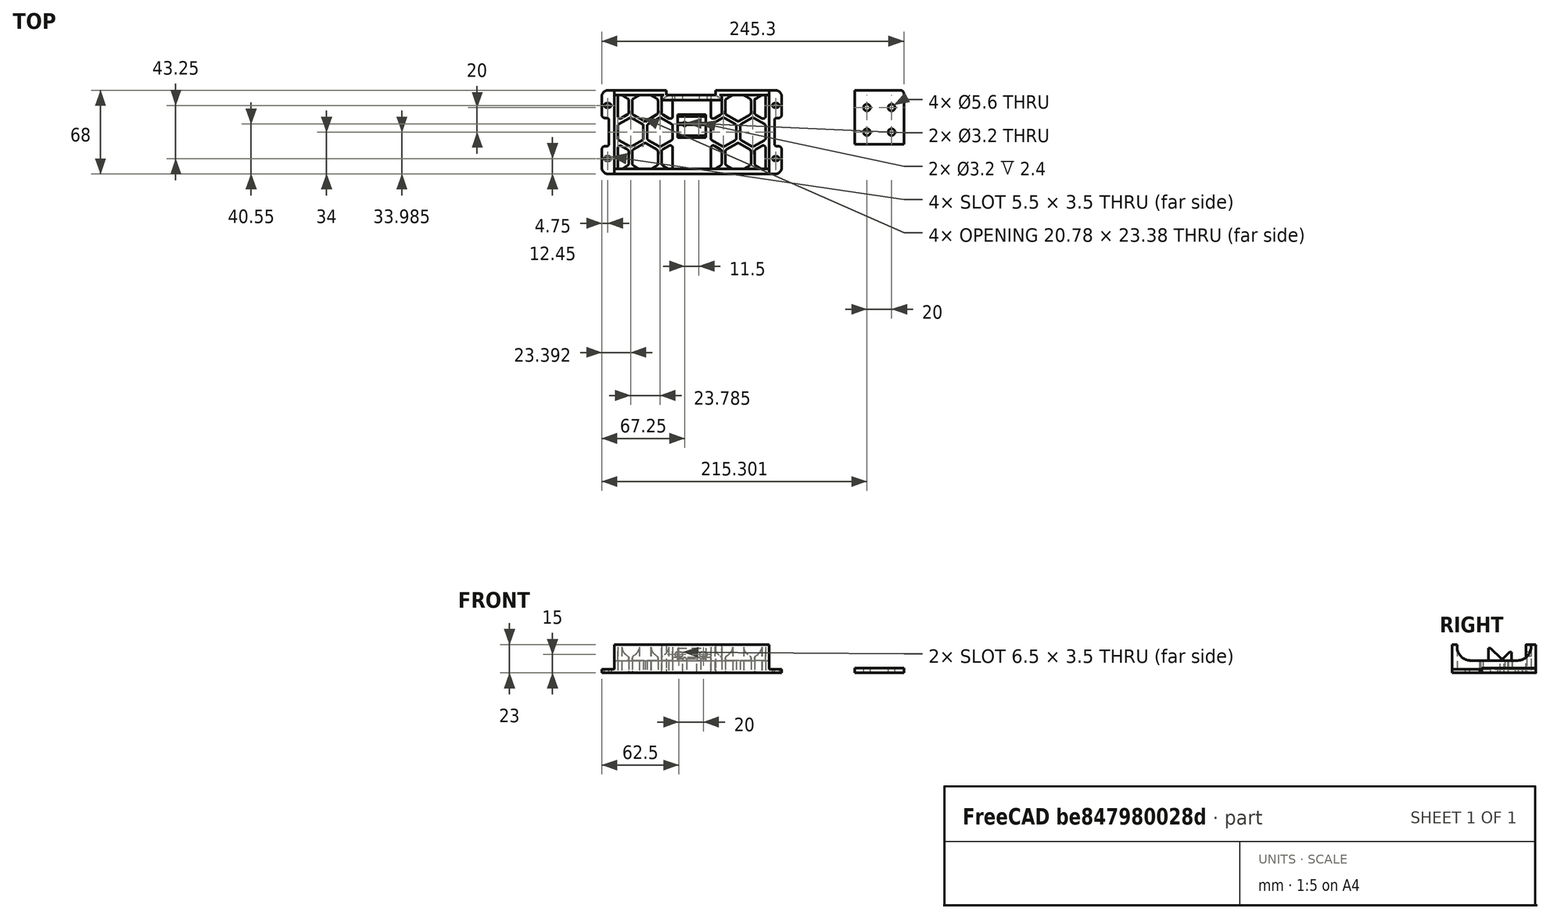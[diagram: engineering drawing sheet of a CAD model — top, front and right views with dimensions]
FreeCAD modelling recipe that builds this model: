
FCSTD DOCUMENT  (FreeCAD 0.19R24291 (Git))
Label: Middle Grill V2
License: All rights reserved
LicenseURL: http://en.wikipedia.org/wiki/All_rights_reserved
objects: Sketcher::SketchObject×10, PartDesign::Pad×5, PartDesign::Pocket×5, Mesh::Feature×4, PartDesign::Body×3, App::DocumentObjectGroup×1, PartDesign::Fillet×1
note: 35 computed .brp shape members not serialized (recipe doc carries the construction recipe); baked Part::Feature solids carry a one-line shape summary decoded from their .brp

FEATURE [Mesh::Feature] grill_front_middle
  Placement = pos=(-37.5,-76,0) rot=(0,0,1;0rad)
FEATURE [Mesh::Feature] grill_front_middle001
  Placement = pos=(-60,-73.5,0) rot=(0,0,1;0rad)
FEATURE [Sketcher::SketchObject] Sketch
  FullyConstrained = true
  MapMode = 5
  Support = -> [XY_Plane]
  sketch-geometry (43):
    g0: LineSegment StartX=5 StartY=0 StartZ=0 EndX=141 EndY=0 EndZ=0
    g1: LineSegment StartX=0 StartY=63 StartZ=0 EndX=0 EndY=48 EndZ=0
    g2: LineSegment StartX=141 StartY=68 StartZ=0 EndX=5 EndY=68 EndZ=0
    g3: ArcOfCircle CenterX=5 CenterY=63 CenterZ=0 NormalX=0 NormalY=0 NormalZ=1 AngleXU=0 Radius=5 StartAngle=1.5708 EndAngle=3.14159
    g4: ArcOfCircle CenterX=5 CenterY=5 CenterZ=0 NormalX=0 NormalY=0 NormalZ=1 AngleXU=0 Radius=5 StartAngle=3.14159 EndAngle=4.71239
    g5: LineSegment StartX=146 StartY=63 StartZ=0 EndX=146 EndY=48 EndZ=0
    g6: ArcOfCircle CenterX=141 CenterY=5 CenterZ=0 NormalX=0 NormalY=0 NormalZ=1 AngleXU=0 Radius=5 StartAngle=4.71239 EndAngle=6.28319
    g7: ArcOfCircle CenterX=141 CenterY=63 CenterZ=0 NormalX=0 NormalY=0 NormalZ=1 AngleXU=0 Radius=5 StartAngle=-9e-16 EndAngle=1.5708
    g8: LineSegment StartX=0 StartY=20 StartZ=0 EndX=0 EndY=5 EndZ=0
    g9: LineSegment StartX=2.5 StartY=22.5 StartZ=0 EndX=4.1 EndY=22.5 EndZ=0
    g10: LineSegment StartX=5.6 StartY=24 StartZ=0 EndX=5.6 EndY=44 EndZ=0
    g11: LineSegment StartX=4.1 StartY=45.5 StartZ=0 EndX=2.5 EndY=45.5 EndZ=0
    g12: ArcOfCircle CenterX=2.5 CenterY=48 CenterZ=0 NormalX=0 NormalY=0 NormalZ=1 AngleXU=0 Radius=2.5 StartAngle=3.14159 EndAngle=4.71239
    g13: ArcOfCircle CenterX=4.1 CenterY=44 CenterZ=0 NormalX=0 NormalY=0 NormalZ=1 AngleXU=0 Radius=1.5 StartAngle=-1.8e-15 EndAngle=1.5708
    g14: ArcOfCircle CenterX=4.1 CenterY=24 CenterZ=0 NormalX=0 NormalY=0 NormalZ=1 AngleXU=0 Radius=1.5 StartAngle=4.71239 EndAngle=6.28319
    g15: ArcOfCircle CenterX=2.5 CenterY=20 CenterZ=0 NormalX=0 NormalY=0 NormalZ=1 AngleXU=0 Radius=2.5 StartAngle=1.5708 EndAngle=3.14159
    g16: LineSegment StartX=143.5 StartY=45.5 StartZ=0 EndX=141.9 EndY=45.5 EndZ=0
    g17: LineSegment StartX=140.4 StartY=44 StartZ=0 EndX=140.4 EndY=24 EndZ=0
    g18: LineSegment StartX=141.9 StartY=22.5 StartZ=0 EndX=143.5 EndY=22.5 EndZ=0
    g19: ArcOfCircle CenterX=143.5 CenterY=48 CenterZ=0 NormalX=0 NormalY=0 NormalZ=1 AngleXU=0 Radius=2.5 StartAngle=4.71239 EndAngle=6.28319
    g20: ArcOfCircle CenterX=141.9 CenterY=44 CenterZ=0 NormalX=0 NormalY=0 NormalZ=1 AngleXU=0 Radius=1.5 StartAngle=1.5708 EndAngle=3.14159
    g21: LineSegment StartX=146 StartY=20 StartZ=0 EndX=146 EndY=5 EndZ=0
    g22: ArcOfCircle CenterX=141.9 CenterY=24 CenterZ=0 NormalX=0 NormalY=0 NormalZ=1 AngleXU=0 Radius=1.5 StartAngle=3.14159 EndAngle=4.71239
    g23: ArcOfCircle CenterX=143.5 CenterY=20 CenterZ=0 NormalX=0 NormalY=0 NormalZ=1 AngleXU=0 Radius=2.5 StartAngle=1e-16 EndAngle=1.5708
    g24: ArcOfCircle CenterX=3.75 CenterY=55.7 CenterZ=0 NormalX=0 NormalY=0 NormalZ=1 AngleXU=0 Radius=1.75 StartAngle=1.5708 EndAngle=4.71239
    g25: ArcOfCircle CenterX=5.75 CenterY=55.7 CenterZ=0 NormalX=0 NormalY=0 NormalZ=1 AngleXU=0 Radius=1.75 StartAngle=4.71239 EndAngle=7.85398
    g26: LineSegment StartX=3.75 StartY=53.95 StartZ=0 EndX=5.75 EndY=53.95 EndZ=0
    g27: LineSegment StartX=3.75 StartY=57.45 StartZ=0 EndX=5.75 EndY=57.45 EndZ=0
    g28: ArcOfCircle CenterX=140.25 CenterY=55.7 CenterZ=0 NormalX=0 NormalY=0 NormalZ=1 AngleXU=0 Radius=1.75 StartAngle=1.5708 EndAngle=4.71239
    g29: ArcOfCircle CenterX=142.25 CenterY=55.7 CenterZ=0 NormalX=0 NormalY=0 NormalZ=1 AngleXU=0 Radius=1.75 StartAngle=4.71239 EndAngle=7.85398
    g30: LineSegment StartX=140.25 StartY=53.95 StartZ=0 EndX=142.25 EndY=53.95 EndZ=0
    g31: LineSegment StartX=140.25 StartY=57.45 StartZ=0 EndX=142.25 EndY=57.45 EndZ=0
    g32: LineSegment StartX=3.75 StartY=57.45 StartZ=0 EndX=140.25 EndY=57.45 EndZ=0
    g33: ArcOfCircle CenterX=3.75 CenterY=12.45 CenterZ=0 NormalX=0 NormalY=0 NormalZ=1 AngleXU=0 Radius=1.75 StartAngle=1.5708 EndAngle=4.71239
    g34: ArcOfCircle CenterX=5.75 CenterY=12.45 CenterZ=0 NormalX=0 NormalY=0 NormalZ=1 AngleXU=0 Radius=1.75 StartAngle=4.71239 EndAngle=7.85398
    g35: LineSegment StartX=3.75 StartY=10.7 StartZ=0 EndX=5.75 EndY=10.7 EndZ=0
    g36: LineSegment StartX=3.75 StartY=14.2 StartZ=0 EndX=5.75 EndY=14.2 EndZ=0
    g37: LineSegment StartX=3.75 StartY=57.45 StartZ=0 EndX=3.75 EndY=14.2 EndZ=0
    g38: ArcOfCircle CenterX=140.25 CenterY=12.45 CenterZ=0 NormalX=0 NormalY=0 NormalZ=1 AngleXU=0 Radius=1.75 StartAngle=1.5708 EndAngle=4.71239
    g39: ArcOfCircle CenterX=142.25 CenterY=12.45 CenterZ=0 NormalX=0 NormalY=0 NormalZ=1 AngleXU=0 Radius=1.75 StartAngle=4.71239 EndAngle=7.85398
    g40: LineSegment StartX=140.25 StartY=10.7 StartZ=0 EndX=142.25 EndY=10.7 EndZ=0
    g41: LineSegment StartX=140.25 StartY=14.2 StartZ=0 EndX=142.25 EndY=14.2 EndZ=0
    g42: LineSegment StartX=3.75 StartY=14.2 StartZ=0 EndX=140.25 EndY=14.2 EndZ=0
  constraints (108):
    c: Horizontal(g0)
    c: Vertical(g1)
    c: Tangent(g1,g3) = -1.5708
    c: Tangent(g2,g3) = -1.5708
    c: Coincident(g8,g4) = -1.5708
    c: Tangent(g0,g4) = -1.5708
    c: PointOnObject(g0,g-1)
    c: PointOnObject(g1,g-2)
    c: DistanceY(g-1,g2) = 68
    c: Radius(g3) = 5
    c: Equal(g3,g4)
    c: Vertical(g5)
    c: Tangent(g0,g6) = -1.5708
    c: Tangent(g5,g7) = 1.5708
    c: Equal(g3,g7)
    c: Equal(g7,g6)
    c: Tangent(g1,g8)
    c: Horizontal(g9)
    c: Vertical(g10)
    c: Horizontal(g11)
    c: Tangent(g1,g12) = -1.5708
    c: Tangent(g11,g12) = 1.5708
    c: Tangent(g11,g13) = -1.5708
    c: Tangent(g10,g13) = -1.5708
    c: Tangent(g10,g14) = -1.5708
    c: Tangent(g9,g14) = -1.5708
    c: Tangent(g9,g15) = 1.5708
    c: Tangent(g8,g15) = -1.5708
    c: Radius(g13) = 1.5
    c: Equal(g13,g14)
    c: Radius(g15) = 2.5
    c: Equal(g15,g12)
    c: DistanceY(g10,g10) = 20
    c: DistanceX(g11,g11) = 1.6
    c: Equal(g8,g1)
    c: Angle(g4) = 1.5708
    c: Vertical(g17)
    c: Horizontal(g16)
    c: Tangent(g16,g19) = 1.5708
    c: Tangent(g5,g19) = 1.5708
    c: Tangent(g16,g20) = -1.5708
    c: Tangent(g17,g20) = -1.5708
    c: Horizontal(g18)
    c: Coincident(g21,g6)
    c: Vertical(g21)
    c: Tangent(g17,g22) = -1.5708
    c: Tangent(g18,g22) = -1.5708
    c: Tangent(g18,g23) = 1.5708
    c: Tangent(g21,g23) = 1.5708
    c: Equal(g12,g19)
    c: Equal(g19,g23)
    c: Equal(g13,g20)
    c: Equal(g20,g22)
    c: Equal(g10,g17)
    c: Equal(g5,g21)
    c: Angle(g6) = 1.5708
    c: DistanceX(g16,g16) = 1.6
    c: Equal(g16,g18)
    c: Tangent(g24,g27) = 1.5708
    c: Tangent(g24,g26) = -1.5708
    c: Tangent(g26,g25) = -1.5708
    c: Tangent(g27,g25) = 1.5708
    c: Horizontal(g26)
    c: Equal(g24,g25)
    c: DistanceY(g-1,g24) = 55.7
    c: DistanceX(g24,g25) = 2
    c: DistanceX(g1,g24) = 3.75
    c: Radius(g25) = 1.75
    c: Tangent(g28,g31) = 1.5708
    c: Tangent(g28,g30) = -1.5708
    c: Tangent(g30,g29) = -1.5708
    c: Tangent(g31,g29) = 1.5708
    c: Horizontal(g30)
    c: Equal(g28,g29)
    c: DistanceX(g28,g29) = 2
    c: Radius(g29) = 1.75
    c: Coincident(g24,g32)
    c: Coincident(g28,g32)
    c: Distance(g32) = 136.5
    c: Angle(g32) = 0
    c: Tangent(g33,g36) = 1.5708
    c: Tangent(g33,g35) = -1.5708
    c: Tangent(g35,g34) = -1.5708
    c: Tangent(g36,g34) = 1.5708
    c: Horizontal(g35)
    c: Equal(g33,g34)
    c: DistanceX(g33,g34) = 2
    c: Radius(g34) = 1.75
    c: Coincident(g24,g37)
    c: Coincident(g33,g37)
    c: Distance(g37) = 43.25
    c: Perpendicular(g37,g32)
    c: Tangent(g38,g41) = 1.5708
    c: Tangent(g38,g40) = -1.5708
    c: Tangent(g40,g39) = -1.5708
    c: Tangent(g41,g39) = 1.5708
    c: Horizontal(g40)
    c: Equal(g38,g39)
    c: DistanceX(g38,g39) = 2
    c: Radius(g39) = 1.75
    c: Coincident(g33,g42)
    c: Coincident(g38,g42)
    c: Equal(g32,g42)
    c: Parallel(g42,g32)
    c: Coincident(g2,g7)
    c: Horizontal(g2)
    c: DistanceX(g2,g2) = 136
    c: Equal(g2,g0)
FEATURE [PartDesign::Pad] Pad  label="Base pad"
  Direction = (1,1,1)
  Length = 3
  Length2 = 100
  Profile = -> Sketch
  Type = 0
FEATURE [Sketcher::SketchObject] Sketch001
  ExternalGeometry = -> [Pad]
  FullyConstrained = true
  MapMode = 5
  Placement = pos=(0,0,3) rot=(0,0,1;0rad)
  Support = -> [Pad]
  sketch-geometry (4):
    g0: LineSegment StartX=10 StartY=68 StartZ=0 EndX=136 EndY=68 EndZ=0
    g1: LineSegment StartX=136 StartY=68 StartZ=0 EndX=136 EndY=0 EndZ=0
    g2: LineSegment StartX=136 StartY=0 StartZ=0 EndX=10 EndY=0 EndZ=0
    g3: LineSegment StartX=10 StartY=0 StartZ=0 EndX=10 EndY=68 EndZ=0
  constraints (13):
    c: Coincident(g0,g1)
    c: Coincident(g1,g2)
    c: Coincident(g2,g3)
    c: Coincident(g3,g0)
    c: Horizontal(g0)
    c: Horizontal(g2)
    c: Vertical(g1)
    c: Vertical(g3)
    c: PointOnObject(g0,g-3)
    c: PointOnObject(g1,g-1)
    c: DistanceX(g-1,g2) = 10
    c: DistanceX(g1,g-4) = 10
    c: DistanceX(g-1,g-4) = 146
FEATURE [PartDesign::Pad] Pad001
  BaseFeature = -> Pad
  Direction = (1,1,1)
  Length = 20
  Length2 = 100
  Profile = -> Sketch001
  Type = 0
FEATURE [Sketcher::SketchObject] Sketch002
  ExternalGeometry = -> [Pad001]
  FullyConstrained = true
  MapMode = 5
  Placement = pos=(10,0,0) rot=(0.57735,-0.57735,-0.57735;2.0944rad)
  Support = -> [Pad001]
  sketch-geometry (6):
    g0: LineSegment StartX=-64 StartY=23 StartZ=0 EndX=-4 EndY=23 EndZ=0
    g1: LineSegment StartX=-4 StartY=23 StartZ=0 EndX=-4 EndY=21 EndZ=0
    g2: LineSegment StartX=-15 StartY=10 StartZ=0 EndX=-53 EndY=10 EndZ=0
    g3: LineSegment StartX=-64 StartY=21 StartZ=0 EndX=-64 EndY=23 EndZ=0
    g4: ArcOfCircle CenterX=-53 CenterY=21 CenterZ=0 NormalX=0 NormalY=0 NormalZ=1 AngleXU=0 Radius=11 StartAngle=3.14159 EndAngle=4.71239
    g5: ArcOfCircle CenterX=-15 CenterY=21 CenterZ=0 NormalX=0 NormalY=0 NormalZ=1 AngleXU=0 Radius=11 StartAngle=4.71239 EndAngle=6.28319
  constraints (16):
    c: Coincident(g0,g1)
    c: Coincident(g3,g0)
    c: Horizontal(g0)
    c: Horizontal(g2)
    c: Vertical(g1)
    c: Vertical(g3)
    c: PointOnObject(g0,g-3)
    c: DistanceX(g0,g-3) = 4
    c: DistanceX(g-3,g0) = 4
    c: Tangent(g3,g4) = 1.5708
    c: Tangent(g2,g4) = 1.5708
    c: Tangent(g2,g5) = 1.5708
    c: Tangent(g1,g5) = 1.5708
    c: Radius(g4) = 11
    c: DistanceY(g-1,g2) = 10
    c: Equal(g4,g5)
FEATURE [PartDesign::Pocket] Pocket
  BaseFeature = -> Pad001
  Length = 130
  Length2 = 100
  Profile = -> Sketch002
  Type = 0
FEATURE [Mesh::Feature] grill_front_left
  Placement = pos=(-155,-76,3) rot=(0,0,1;0rad)
FEATURE [Mesh::Feature] grill_front_right
  Placement = pos=(81,-76,3) rot=(0,0,1;0rad)
FEATURE [Sketcher::SketchObject] Sketch003
  FullyConstrained = true
  MapMode = 5
  Placement = pos=(0,0,0) rot=(0.57735,0.57735,0.57735;2.0944rad)
  Support = -> [YZ_Plane001]
  sketch-geometry (8):
    g0: LineSegment StartX=29.5 StartY=10 StartZ=0 EndX=29.5 EndY=20.15 EndZ=0
    g1: LineSegment StartX=29.5 StartY=20.15 StartZ=0 EndX=31.2 EndY=20.15 EndZ=0
    g2: LineSegment StartX=31.2 StartY=20.15 StartZ=0 EndX=39.95 EndY=11.4 EndZ=0
    g3: LineSegment StartX=39.95 StartY=11.4 StartZ=0 EndX=41.15 EndY=11.4 EndZ=0
    g4: LineSegment StartX=41.15 StartY=11.4 StartZ=0 EndX=46.55 EndY=16.8 EndZ=0
    g5: LineSegment StartX=46.55 StartY=16.8 StartZ=0 EndX=48.25 EndY=16.8 EndZ=0
    g6: LineSegment StartX=48.25 StartY=16.8 StartZ=0 EndX=48.25 EndY=10 EndZ=0
    g7: LineSegment StartX=48.25 StartY=10 StartZ=0 EndX=29.5 EndY=10 EndZ=0
  constraints (24):
    c: Vertical(g0)
    c: Coincident(g0,g1)
    c: Horizontal(g1)
    c: Coincident(g1,g2)
    c: Coincident(g2,g3)
    c: Coincident(g3,g4)
    c: Coincident(g4,g5)
    c: Horizontal(g5)
    c: Coincident(g5,g6)
    c: Vertical(g6)
    c: Coincident(g6,g7)
    c: Coincident(g7,g0)
    c: Horizontal(g7)
    c: DistanceY(g-1,g0) = 10
    c: DistanceX(g0,g5) = 18.75
    c: DistanceX(g-1,g0) = 29.5
    c: DistanceX(g1,g1) = 1.7
    c: DistanceX(g5,g5) = 1.7
    c: DistanceX(g3,g3) = 1.2
    c: Angle(g1,g2) = 2.35619
    c: Angle(g4,g5) = 2.35619
    c: DistanceY(g0,g2) = 1.4
    c: Horizontal(g3)
    c: DistanceY(g6,g6) = 6.8
FEATURE [PartDesign::Pad] Pad002
  Direction = (1,1,1)
  Length = 23
  Length2 = 100
  Placement = pos=(0,0,0) rot=(0.57735,0.57735,0.57735;2.0944rad)
  Profile = -> Sketch003
  Type = 0
FEATURE [Sketcher::SketchObject] Sketch004
  ExternalGeometry = -> [Pad002]
  FullyConstrained = true
  MapMode = 5
  Placement = pos=(-3.9e-15,5.6e-15,10) rot=(0.707107,0.707107,0;3.14159rad)
  Support = -> [Pad002]
  sketch-geometry (2):
    g0: Circle CenterX=40.55 CenterY=5.75 CenterZ=0 NormalX=0 NormalY=0 NormalZ=1 AngleXU=0 Radius=1.6
    g1: Circle CenterX=40.55 CenterY=17.25 CenterZ=0 NormalX=0 NormalY=0 NormalZ=1 AngleXU=0 Radius=1.6
  constraints (6):
    c: Radius(g0) = 1.6
    c: Equal(g0,g1)
    c: Vertical(g0,g1)
    c: DistanceY(g1,g-3) = 5.75
    c: DistanceY(g0,g1) = 11.5
    c: DistanceX(g-3,g0) = 0.6
FEATURE [PartDesign::Pocket] Pocket001
  BaseFeature = -> Pad002
  Length = 5
  Length2 = 100
  Placement = pos=(0,0,0) rot=(0.57735,0.57735,0.57735;2.0944rad)
  Profile = -> Sketch004
  Type = 0
FEATURE [PartDesign::Body] Body001
  Group = -> [Sketch003,Pad002,Sketch004,Pocket001]
  Origin = -> Origin001
  Placement = pos=(61.5,0,0) rot=(0,0,1;0rad)
  Tip = -> Pocket001
FEATURE [Sketcher::SketchObject] Sketch005
  ExternalGeometry = -> [Pocket]
  FullyConstrained = false
  MapMode = 5
  Placement = pos=(0,0,10) rot=(0,0,1;0rad)
  Support = -> [Pocket]
  sketch-geometry (104):
    g0: Circle CenterX=67.25 CenterY=40.55 CenterZ=0 NormalX=0 NormalY=0 NormalZ=1 AngleXU=0 Radius=1.6
    g1: Circle CenterX=78.75 CenterY=40.55 CenterZ=0 NormalX=0 NormalY=0 NormalZ=1 AngleXU=0 Radius=1.6
    g2: LineSegment StartX=36.7846 StartY=28 StartZ=0 EndX=47.1769 EndY=22 EndZ=0
    g3: LineSegment StartX=47.1769 StartY=22 StartZ=0 EndX=57.5692 EndY=28 EndZ=0
    g4: LineSegment StartX=57.5692 StartY=28 StartZ=0 EndX=57.5692 EndY=40 EndZ=0
    g5: LineSegment StartX=57.5692 StartY=40 StartZ=0 EndX=47.1769 EndY=46 EndZ=0
    g6: LineSegment StartX=47.1769 StartY=46 StartZ=0 EndX=36.7846 EndY=40 EndZ=0
    g7: LineSegment StartX=36.7846 StartY=40 StartZ=0 EndX=36.7846 EndY=28 EndZ=0
    g8: Circle CenterX=47.1769 CenterY=34 CenterZ=0 NormalX=0 NormalY=0 NormalZ=1 AngleXU=0 Radius=12
    g9: LineSegment StartX=13 StartY=28 StartZ=0 EndX=23.3923 EndY=22 EndZ=0
    g10: LineSegment StartX=23.3923 StartY=22 StartZ=0 EndX=33.7846 EndY=28 EndZ=0
    g11: LineSegment StartX=33.7846 StartY=28 StartZ=0 EndX=33.7846 EndY=40 EndZ=0
    g12: LineSegment StartX=33.7846 StartY=40 StartZ=0 EndX=23.3923 EndY=46 EndZ=0
    g13: LineSegment StartX=23.3923 StartY=46 StartZ=0 EndX=13 EndY=40 EndZ=0
    g14: LineSegment StartX=13 StartY=40 StartZ=0 EndX=13 EndY=28 EndZ=0
    g15: Circle CenterX=23.3923 CenterY=34 CenterZ=0 NormalX=0 NormalY=0 NormalZ=1 AngleXU=0 Radius=12
    g16: LineSegment StartX=112.215 StartY=28 StartZ=0 EndX=122.608 EndY=22 EndZ=0
    g17: LineSegment StartX=122.608 StartY=22 StartZ=0 EndX=133 EndY=28 EndZ=0
    g18: LineSegment StartX=133 StartY=28 StartZ=0 EndX=133 EndY=40 EndZ=0
    g19: LineSegment StartX=133 StartY=40 StartZ=0 EndX=122.608 EndY=46 EndZ=0
    g20: LineSegment StartX=122.608 StartY=46 StartZ=0 EndX=112.215 EndY=40 EndZ=0
    g21: LineSegment StartX=112.215 StartY=40 StartZ=0 EndX=112.215 EndY=28 EndZ=0
    g22: Circle CenterX=122.608 CenterY=34 CenterZ=0 NormalX=0 NormalY=0 NormalZ=1 AngleXU=0 Radius=12
    g23: LineSegment StartX=88.4308 StartY=28 StartZ=0 EndX=98.8231 EndY=22 EndZ=0
    g24: LineSegment StartX=98.8231 StartY=22 StartZ=0 EndX=109.215 EndY=28 EndZ=0
    g25: LineSegment StartX=109.215 StartY=28 StartZ=0 EndX=109.215 EndY=40 EndZ=0
    g26: LineSegment StartX=109.215 StartY=40 StartZ=0 EndX=98.8231 EndY=46 EndZ=0
    g27: LineSegment StartX=98.8231 StartY=46 StartZ=0 EndX=88.4308 EndY=40 EndZ=0
    g28: LineSegment StartX=88.4308 StartY=40 StartZ=0 EndX=88.4308 EndY=28 EndZ=0
    g29: Circle CenterX=98.8231 CenterY=34 CenterZ=0 NormalX=0 NormalY=0 NormalZ=1 AngleXU=0 Radius=12
    g30: LineSegment StartX=24.75 StartY=7.32481 StartZ=0 EndX=30.3742 EndY=4 EndZ=0
    g31: LineSegment StartX=39.9104 StartY=4 StartZ=0 EndX=45.5346 EndY=7.32481 EndZ=0
    g32: LineSegment StartX=45.5346 StartY=7.32481 StartZ=0 EndX=45.5346 EndY=19.3248 EndZ=0
    g33: LineSegment StartX=45.5346 StartY=19.3248 StartZ=0 EndX=35.1423 EndY=25.3248 EndZ=0
    g34: LineSegment StartX=35.1423 StartY=25.3248 StartZ=0 EndX=24.75 EndY=19.3248 EndZ=0
    g35: LineSegment StartX=24.75 StartY=19.3248 StartZ=0 EndX=24.75 EndY=7.32481 EndZ=0
    g36: Circle CenterX=35.1423 CenterY=13.3248 CenterZ=0 NormalX=0 NormalY=0 NormalZ=1 AngleXU=0 Radius=12
    g37: LineSegment StartX=30.3742 StartY=4 StartZ=0 EndX=39.9104 EndY=4 EndZ=0
    g38: LineSegment StartX=115.215 StartY=4 StartZ=0 EndX=121.108 EndY=7.40192 EndZ=0
    g39: LineSegment StartX=121.108 StartY=7.40192 StartZ=0 EndX=121.108 EndY=19.4019 EndZ=0
    g40: LineSegment StartX=121.108 StartY=19.4019 StartZ=0 EndX=110.715 EndY=25.4019 EndZ=0
    g41: LineSegment StartX=110.715 StartY=25.4019 StartZ=0 EndX=100.323 EndY=19.4019 EndZ=0
    g42: LineSegment StartX=100.323 StartY=19.4019 StartZ=0 EndX=100.323 EndY=7.40192 EndZ=0
    g43: LineSegment StartX=100.323 StartY=7.40192 StartZ=0 EndX=106.215 EndY=4 EndZ=0
    g44: Circle CenterX=110.715 CenterY=13.4019 CenterZ=0 NormalX=0 NormalY=0 NormalZ=1 AngleXU=0 Radius=12
    g45: LineSegment StartX=110.715 StartY=42.5981 StartZ=0 EndX=121.108 EndY=48.5981 EndZ=0
    g46: LineSegment StartX=121.108 StartY=48.5981 StartZ=0 EndX=121.108 EndY=60.5981 EndZ=0
    g47: LineSegment StartX=121.108 StartY=60.5981 StartZ=0 EndX=115.215 EndY=64 EndZ=0
    g48: LineSegment StartX=106.215 StartY=64 StartZ=0 EndX=100.323 EndY=60.5981 EndZ=0
    g49: LineSegment StartX=100.323 StartY=60.5981 StartZ=0 EndX=100.323 EndY=48.5981 EndZ=0
    g50: LineSegment StartX=100.323 StartY=48.5981 StartZ=0 EndX=110.715 EndY=42.5981 EndZ=0
    g51: Circle CenterX=110.715 CenterY=54.5981 CenterZ=0 NormalX=0 NormalY=0 NormalZ=1 AngleXU=0 Radius=12
    g52: LineSegment StartX=45.5346 StartY=48.6752 StartZ=0 EndX=45.5346 EndY=60.6752 EndZ=0
    g53: LineSegment StartX=45.5346 StartY=60.6752 StartZ=0 EndX=39.7759 EndY=64 EndZ=0
    g54: LineSegment StartX=30.5087 StartY=64 StartZ=0 EndX=24.75 EndY=60.6752 EndZ=0
    g55: LineSegment StartX=24.75 StartY=60.6752 StartZ=0 EndX=24.75 EndY=48.6752 EndZ=0
    g56: LineSegment StartX=24.75 StartY=48.6752 StartZ=0 EndX=35.1423 EndY=42.6752 EndZ=0
    g57: LineSegment StartX=35.1423 StartY=42.6752 StartZ=0 EndX=45.5346 EndY=48.6752 EndZ=0
    g58: Circle CenterX=35.1423 CenterY=54.6752 CenterZ=0 NormalX=0 NormalY=0 NormalZ=1 AngleXU=0 Radius=12
    g59: LineSegment StartX=106.215 StartY=4 StartZ=0 EndX=115.215 EndY=4 EndZ=0
    g60: LineSegment StartX=106.215 StartY=64 StartZ=0 EndX=115.215 EndY=64 EndZ=0
    g61: LineSegment StartX=30.5087 StartY=64 StartZ=0 EndX=39.7759 EndY=64 EndZ=0
    g62: LineSegment StartX=48.5346 StartY=60.6752 StartZ=0 EndX=48.5346 EndY=48.6752 EndZ=0
    g63: LineSegment StartX=48.5346 StartY=48.6752 StartZ=0 EndX=57.5692 EndY=43.4591 EndZ=0
    g64: LineSegment StartX=57.5692 StartY=43.4591 StartZ=0 EndX=57.5692 EndY=64 EndZ=0
    g65: LineSegment StartX=57.5692 StartY=64 StartZ=0 EndX=54.2933 EndY=64 EndZ=0
    g66: LineSegment StartX=-7.51848 StartY=64 StartZ=0 EndX=146.679 EndY=64 EndZ=0
    g67: LineSegment StartX=124.108 StartY=48.5981 StartZ=0 EndX=133 EndY=43.4641 EndZ=0
    g68: LineSegment StartX=124.108 StartY=60.5981 StartZ=0 EndX=124.108 EndY=48.5981 EndZ=0
    g69: LineSegment StartX=133 StartY=64 StartZ=0 EndX=130 EndY=64 EndZ=0
    g70: LineSegment StartX=133 StartY=43.4641 StartZ=0 EndX=133 EndY=64 EndZ=0
    g71: LineSegment StartX=48.5346 StartY=60.6752 StartZ=0 EndX=54.2933 EndY=64 EndZ=0
    g72: LineSegment StartX=124.108 StartY=60.5981 StartZ=0 EndX=130 EndY=64 EndZ=0
    g73: LineSegment StartX=-5.57796 StartY=4 StartZ=0 EndX=155.374 EndY=4 EndZ=0
    g74: LineSegment StartX=48.5346 StartY=19.3248 StartZ=0 EndX=57.5692 EndY=24.5409 EndZ=0
    g75: LineSegment StartX=57.5692 StartY=24.5409 StartZ=0 EndX=57.5692 EndY=4 EndZ=0
    g76: LineSegment StartX=57.5692 StartY=4 StartZ=0 EndX=54.2933 EndY=4 EndZ=0
    g77: LineSegment StartX=54.2933 StartY=4 StartZ=0 EndX=48.5346 EndY=7.32481 EndZ=0
    g78: LineSegment StartX=48.5346 StartY=7.32481 StartZ=0 EndX=48.5346 EndY=19.3248 EndZ=0
    g79: LineSegment StartX=13 StartY=43.6234 StartZ=0 EndX=13 EndY=64 EndZ=0
    g80: LineSegment StartX=13 StartY=64 StartZ=0 EndX=16.2759 EndY=64 EndZ=0
    g81: LineSegment StartX=16.2759 StartY=64 StartZ=0 EndX=21.75 EndY=60.6752 EndZ=0
    g82: LineSegment StartX=21.75 StartY=60.6752 StartZ=0 EndX=21.75 EndY=48.6752 EndZ=0
    g83: LineSegment StartX=21.75 StartY=48.6752 StartZ=0 EndX=13 EndY=43.6234 EndZ=0
    g84: LineSegment StartX=13 StartY=4 StartZ=0 EndX=13 EndY=24.3766 EndZ=0
    g85: LineSegment StartX=13 StartY=24.3766 StartZ=0 EndX=21.75 EndY=19.3248 EndZ=0
    g86: LineSegment StartX=21.75 StartY=19.3248 StartZ=0 EndX=21.75 EndY=7.32481 EndZ=0
    g87: LineSegment StartX=21.75 StartY=7.32481 StartZ=0 EndX=16.2759 EndY=4 EndZ=0
    g88: LineSegment StartX=16.2759 StartY=4 StartZ=0 EndX=13 EndY=4 EndZ=0
    g89: LineSegment StartX=88.4308 StartY=64 StartZ=0 EndX=88.4308 EndY=43.4641 EndZ=0
    g90: LineSegment StartX=88.4308 StartY=43.4641 StartZ=0 EndX=97.3231 EndY=48.5981 EndZ=0
    g91: LineSegment StartX=97.3231 StartY=48.5981 StartZ=0 EndX=97.3231 EndY=60.5981 EndZ=0
    g92: LineSegment StartX=97.3231 StartY=60.5981 StartZ=0 EndX=91.7067 EndY=64 EndZ=0
    g93: LineSegment StartX=91.7067 StartY=64 StartZ=0 EndX=88.4308 EndY=64 EndZ=0
    g94: LineSegment StartX=88.4308 StartY=24.5359 StartZ=0 EndX=88.4308 EndY=4 EndZ=0
    g95: LineSegment StartX=88.4308 StartY=4 StartZ=0 EndX=91.7067 EndY=4 EndZ=0
    g96: LineSegment StartX=91.7067 StartY=4 StartZ=0 EndX=97.3231 EndY=7.40192 EndZ=0
    g97: LineSegment StartX=97.3231 StartY=7.40192 StartZ=0 EndX=97.3231 EndY=19.4019 EndZ=0
    g98: LineSegment StartX=97.3231 StartY=19.4019 StartZ=0 EndX=88.4308 EndY=24.5359 EndZ=0
    g99: LineSegment StartX=124.108 StartY=19.4019 StartZ=0 EndX=124.108 EndY=7.40192 EndZ=0
    g100: LineSegment StartX=124.108 StartY=7.40192 StartZ=0 EndX=129.724 EndY=4 EndZ=0
    g101: LineSegment StartX=129.724 StartY=4 StartZ=0 EndX=133 EndY=4 EndZ=0
    g102: LineSegment StartX=133 StartY=4 StartZ=0 EndX=133 EndY=24.5359 EndZ=0
    g103: LineSegment StartX=133 StartY=24.5359 StartZ=0 EndX=124.108 EndY=19.4019 EndZ=0
  constraints (294):
    c: Radius(g0) = 1.6
    c: Equal(g0,g1)
    c: Horizontal(g0,g1)
    c: DistanceX(g0,g1) = 11.5
    c: DistanceY(g-1,g0) = 40.55
    c: DistanceX(g-1,g0) = 67.25
    c: Coincident(g2,g3)
    c: Coincident(g3,g4)
    c: Coincident(g4,g5)
    c: Coincident(g5,g6)
    c: Coincident(g6,g7)
    c: Coincident(g7,g2)
    c: Equal(g2, g3-g7) x5
    c: PointOnObject(g2,g8)
    c: PointOnObject(g3,g8)
    c: PointOnObject(g4,g8)
    c: PointOnObject(g5,g8)
    c: PointOnObject(g6,g8)
    c: PointOnObject(g7,g8)
    c: Vertical(g7)
    c: DistanceY(g2,g5) = 24
    c: Coincident(g9,g10)
    c: Coincident(g10,g11)
    c: Coincident(g11,g12)
    c: Coincident(g12,g13)
    c: Coincident(g13,g14)
    c: Coincident(g14,g9)
    c: Equal(g9, g10-g14) x5
    c: PointOnObject(g9,g15)
    c: PointOnObject(g10,g15)
    c: PointOnObject(g11,g15)
    c: PointOnObject(g12,g15)
    c: PointOnObject(g13,g15)
    c: PointOnObject(g14,g15)
    c: Vertical(g14)
    c: DistanceX(g11,g6) = 3
    c: Horizontal(g15,g8)
    c: DistanceY(g-1,g15) = 34
    c: DistanceX(g-1,g9) = 13
    c: Coincident(g16,g17)
    c: Coincident(g17,g18)
    c: Coincident(g18,g19)
    c: Coincident(g19,g20)
    c: Coincident(g20,g21)
    c: Coincident(g21,g16)
    c: Equal(g16, g17-g21) x5
    c: PointOnObject(g16,g22)
    c: PointOnObject(g17,g22)
    c: PointOnObject(g18,g22)
    c: PointOnObject(g19,g22)
    c: PointOnObject(g20,g22)
    c: PointOnObject(g21,g22)
    c: Vertical(g21)
    c: DistanceY(g16,g19) = 24
    c: Coincident(g23,g24)
    c: Coincident(g24,g25)
    c: Coincident(g25,g26)
    c: Coincident(g26,g27)
    c: Coincident(g27,g28)
    c: Coincident(g28,g23)
    c: Equal(g23, g24-g28) x5
    c: PointOnObject(g23,g29)
    c: PointOnObject(g24,g29)
    c: PointOnObject(g25,g29)
    c: PointOnObject(g26,g29)
    c: PointOnObject(g27,g29)
    c: PointOnObject(g28,g29)
    c: Vertical(g28)
    c: DistanceX(g25,g20) = 3
    c: Horizontal(g29,g22)
    c: DistanceX(g17,g-3) = 13
    c: DistanceY(g-1,g29) = 34
    c: Coincident(g31,g32)
    c: Coincident(g32,g33)
    c: Coincident(g33,g34)
    c: Coincident(g34,g35)
    c: Coincident(g35,g30)
    c: PointOnObject(g31,g36)
    c: PointOnObject(g32,g36)
    c: PointOnObject(g33,g36)
    c: PointOnObject(g34,g36)
    c: PointOnObject(g35,g36)
    c: Vertical(g35)
    c: Distance(g10,g33) = 3
    c: DistanceX(g15,g36) = 11.75
    c: Horizontal(g37)
    c: Coincident(g30,g37)
    c: Coincident(g31,g37)
    c: Coincident(g38,g39)
    c: Coincident(g39,g40)
    c: Coincident(g40,g41)
    c: Coincident(g41,g42)
    c: Coincident(g42,g43)
    c: PointOnObject(g38,g44)
    c: PointOnObject(g39,g44)
    c: PointOnObject(g40,g44)
    c: PointOnObject(g41,g44)
    c: PointOnObject(g42,g44)
    c: Coincident(g45,g46)
    c: Coincident(g46,g47)
    c: Coincident(g48,g49)
    c: Coincident(g49,g50)
    c: Coincident(g50,g45)
    c: Equal(g45,g46)
    c: Equal(g45,g49)
    c: Equal(g45,g50)
    c: PointOnObject(g45,g51)
    c: PointOnObject(g46,g51)
    c: PointOnObject(g48,g51)
    c: PointOnObject(g49,g51)
    c: PointOnObject(g50,g51)
    c: Coincident(g52,g53)
    c: Coincident(g54,g55)
    c: Coincident(g55,g56)
    c: Coincident(g56,g57)
    c: Coincident(g57,g52)
    c: Equal(g52,g55)
    c: Equal(g52,g56)
    c: Equal(g52,g57)
    c: PointOnObject(g52,g58)
    c: PointOnObject(g54,g58)
    c: PointOnObject(g55,g58)
    c: PointOnObject(g56,g58)
    c: PointOnObject(g57,g58)
    c: Vertical(g42)
    c: Vertical(g49)
    c: Vertical(g55)
    c: Vertical(g58,g36)
    c: Distance(g11,g56) = 3
    c: Equal(g8,g36)
    c: Equal(g8,g51)
    c: Equal(g51,g44)
    c: Equal(g8,g58)
    c: Equal(g30,g31)
    c: Vertical(g32)
    c: Equal(g34,g33)
    c: Vertical(g33,g36)
    c: Angle(g30,g35) = 2.10469
    c: Equal(g4,g32)
    c: Vertical(g44,g51)
    c: Distance(g24,g40) = 3
    c: Distance(g39,g16) = 3
    c: Distance(g25,g45) = 3
    c: Horizontal(g59)
    c: Coincident(g43,g59)
    c: Coincident(g38,g59)
    c: Horizontal(g60)
    c: Distance(g45,g19) = 3
    c: Coincident(g48,g60)
    c: Coincident(g47,g60)
    c: Horizontal(g61)
    c: Coincident(g54,g61)
    c: Coincident(g53,g61)
    c: Vertical(g62)
    c: Coincident(g62,g63)
    c: Coincident(g63,g64)
    c: Vertical(g64)
    c: Coincident(g64,g65)
    c: Horizontal(g65)
    c: Horizontal(g66)
    c: DistanceY(g66,g-4) = 4
    c: PointOnObject(g54,g66)
    c: Parallel(g63,g5)
    c: DistanceX(g52,g62) = 3
    c: Vertical(g52)
    c: Vertical(g4,g63)
    c: Horizontal(g52,g62)
    c: Vertical(g68)
    c: Coincident(g68,g67)
    c: Coincident(g67,g70)
    c: Vertical(g70)
    c: Coincident(g70,g69)
    c: Horizontal(g69)
    c: Horizontal(g45,g67)
    c: Vertical(g67,g18)
    c: PointOnObject(g69,g66)
    c: PointOnObject(g47,g66)
    c: Vertical(g46)
    c: DistanceX(g45,g67) = 3
    c: Parallel(g67,g19)
    c: Angle(g53,g52) = 2.0944
    c: Coincident(g62,g71)
    c: Coincident(g65,g71)
    c: Angle(g62,g71) = 2.0944
    c: PointOnObject(g65,g66)
    c: Horizontal(g52,g62)
    c: Angle(g68,g72) = 2.0944
    c: Coincident(g68,g72)
    c: Coincident(g69,g72)
    c: Angle(g47,g46) = 2.0944
    c: Horizontal(g46,g68)
    c: Equal(g47,g48)
    c: Equal(g8,g29)
    c: Equal(g53,g54)
    c: Equal(g41,g24)
    c: Parallel(g41,g24)
    c: Equal(g42,g39)
    c: Angle(g43,g42) = 2.0944
    c: Equal(g43,g38)
    c: Horizontal(g73)
    c: DistanceY(g-1,g73) = 4
    c: PointOnObject(g30,g73)
    c: PointOnObject(g38,g73)
    c: Equal(g8,g15)
    c: Coincident(g74,g75)
    c: PointOnObject(g75,g73)
    c: Vertical(g75)
    c: Coincident(g75,g76)
    c: PointOnObject(g76,g73)
    c: Coincident(g76,g77)
    c: Coincident(g77,g78)
    c: Coincident(g78,g74)
    c: Vertical(g78)
    c: Vertical(g3,g74)
    c: Parallel(g74,g3)
    c: Horizontal(g32,g74)
    c: Horizontal(g31,g77)
    c: DistanceX(g32,g74) = 3
    c: Equal(g65,g76)
    c: PointOnObject(g79,g66)
    c: Vertical(g79)
    c: Coincident(g79,g80)
    c: PointOnObject(g80,g66)
    c: Coincident(g80,g81)
    c: Coincident(g81,g82)
    c: Vertical(g82)
    c: Coincident(g82,g83)
    c: Coincident(g83,g79)
    c: PointOnObject(g84,g73)
    c: Vertical(g84)
    c: Coincident(g84,g85)
    c: Coincident(g85,g86)
    c: Vertical(g86)
    c: Coincident(g86,g87)
    c: PointOnObject(g87,g73)
    c: Coincident(g87,g88)
    c: Coincident(g88,g84)
    c: Vertical(g13,g79)
    c: Vertical(g79,g84)
    c: Parallel(g83,g13)
    c: Parallel(g9,g85)
    c: Equal(g65,g80)
    c: Equal(g80,g88)
    c: Horizontal(g55,g82)
    c: Horizontal(g54,g81)
    c: DistanceX(g82,g55) = 3
    c: DistanceX(g85,g34) = 3
    c: Horizontal(g34,g85)
    c: Horizontal(g30,g86)
    c: PointOnObject(g89,g66)
    c: Vertical(g89)
    c: Coincident(g89,g90)
    c: Coincident(g90,g91)
    c: Vertical(g91)
    c: Coincident(g91,g92)
    c: PointOnObject(g92,g66)
    c: Coincident(g92,g93)
    c: Coincident(g93,g89)
    c: PointOnObject(g94,g73)
    c: Vertical(g94)
    c: Coincident(g94,g95)
    c: PointOnObject(g95,g73)
    c: Coincident(g95,g96)
    c: Coincident(g96,g97)
    c: Vertical(g97)
    c: Coincident(g97,g98)
    c: Coincident(g98,g94)
    c: Vertical(g99)
    c: Coincident(g99,g100)
    c: PointOnObject(g100,g73)
    c: Coincident(g100,g101)
    c: PointOnObject(g101,g73)
    c: Coincident(g101,g102)
    c: Vertical(g102)
    c: Coincident(g102,g103)
    c: Coincident(g103,g99)
    c: Equal(g65,g93)
    c: Equal(g93,g95)
    c: Equal(g95,g101)
    c: Vertical(g17,g102)
    c: Horizontal(g99,g38)
    c: Horizontal(g99,g39)
    c: DistanceX(g39,g99) = 3
    c: Equal(g70,g102)
    c: Equal(g102,g89)
    c: Equal(g89,g94)
    c: Vertical(g23,g94)
    c: Vertical(g94,g89)
    c: Horizontal(g96,g42)
    c: Horizontal(g97,g41)
    c: DistanceX(g97,g41) = 3
    c: DistanceX(g90,g49) = 3
    c: Horizontal(g90,g49)
    c: Horizontal(g48,g91)
FEATURE [PartDesign::Pocket] Pocket002
  BaseFeature = -> Pocket
  Length = 10
  Length2 = 20
  Profile = -> Sketch005
  Type = 4
FEATURE [App::DocumentObjectGroup] Group  label="Grill STLS"
  Group = -> [grill_front_left,grill_front_right,grill_front_middle001,grill_front_middle]
FEATURE [Sketcher::SketchObject] Sketch006
  ExternalGeometry = -> [Pad]
  FullyConstrained = true
  MapMode = 5
  Placement = pos=(0,0,3) rot=(0,0,1;0rad)
  Support = -> [Pad]
  sketch-geometry (4):
    g0: LineSegment StartX=48.5 StartY=64 StartZ=0 EndX=97.5 EndY=64 EndZ=0
    g1: LineSegment StartX=97.5 StartY=64 StartZ=0 EndX=97.5 EndY=60 EndZ=0
    g2: LineSegment StartX=97.5 StartY=60 StartZ=0 EndX=48.5 EndY=60 EndZ=0
    g3: LineSegment StartX=48.5 StartY=60 StartZ=0 EndX=48.5 EndY=64 EndZ=0
  constraints (12):
    c: Coincident(g0,g1)
    c: Coincident(g1,g2)
    c: Coincident(g2,g3)
    c: Coincident(g3,g0)
    c: Horizontal(g0)
    c: Horizontal(g2)
    c: Vertical(g1)
    c: Vertical(g3)
    c: DistanceY(g1,g1) = 4
    c: DistanceX(g2,g2) = 49
    c: DistanceY(g0,g-3) = 4
    c: DistanceX(g-1,g2) = 48.5
FEATURE [PartDesign::Pad] Pad003
  BaseFeature = -> Pocket002
  Direction = (1,1,1)
  Length = 20
  Length2 = 2.98
  Profile = -> Sketch006
  Type = 4
FEATURE [Sketcher::SketchObject] Sketch007
  ExternalGeometry = -> [Pad003]
  FullyConstrained = false
  MapMode = 5
  Placement = pos=(0,0,23) rot=(0,0,1;0rad)
  Support = -> [Pad003]
  sketch-geometry (4):
    g0: LineSegment StartX=52.5 StartY=68 StartZ=0 EndX=92.2765 EndY=68 EndZ=0
    g1: LineSegment StartX=92.2765 StartY=68 StartZ=0 EndX=92.2765 EndY=64 EndZ=0
    g2: LineSegment StartX=92.2765 StartY=64 StartZ=0 EndX=52.5 EndY=64 EndZ=0
    g3: LineSegment StartX=52.5 StartY=64 StartZ=0 EndX=52.5 EndY=68 EndZ=0
  constraints (11):
    c: Coincident(g0,g1)
    c: Coincident(g1,g2)
    c: Coincident(g2,g3)
    c: Coincident(g3,g0)
    c: Horizontal(g0)
    c: Horizontal(g2)
    c: Vertical(g1)
    c: Vertical(g3)
    c: PointOnObject(g0,g-3)
    c: DistanceY(g1,g1) = 4
    c: DistanceX(g-1,g2) = 52.5
FEATURE [PartDesign::Pocket] Pocket003  label="Top 4040 Cutout"
  BaseFeature = -> Pad003
  Length = 30
  Length2 = 100
  Profile = -> Sketch007
  Type = 0
FEATURE [PartDesign::Fillet] Fillet
  Base = -> Pocket003 [Edge477,Edge475,Edge408,Edge404,Edge431,Edge436,Edge420,Edge360,Edge356,Edge394,Edge209,Edge309,Edge303,Edge295,Edge416,Edge275,Edge344,Edge348,Edge389,Edge370,Edge351,Edge352,Edge339,Edge340,Edge346,Edge342,Edge369,Edge257,Edge194,Edge411,Edge399,Edge198,Edge433,Edge445,Edge285,Edge358,Edge406,Edge418,Edge354,Edge271,+21 more]
  BaseFeature = -> Pocket003
  Radius = 2
  SupportTransform = false
FEATURE [Sketcher::SketchObject] Sketch008
  FullyConstrained = true
  MapMode = 5
  Placement = pos=(0,64,0) rot=(0,0.707107,0.707107;3.14159rad)
  Support = -> [Fillet]
  sketch-geometry (8):
    g0: ArcOfCircle CenterX=-84 CenterY=15 CenterZ=0 NormalX=0 NormalY=0 NormalZ=1 AngleXU=0 Radius=1.75 StartAngle=1.5708 EndAngle=4.71239
    g1: ArcOfCircle CenterX=-81 CenterY=15 CenterZ=0 NormalX=0 NormalY=0 NormalZ=1 AngleXU=0 Radius=1.75 StartAngle=4.71239 EndAngle=7.85398
    g2: LineSegment StartX=-84 StartY=13.25 StartZ=0 EndX=-81 EndY=13.25 EndZ=0
    g3: LineSegment StartX=-84 StartY=16.75 StartZ=0 EndX=-81 EndY=16.75 EndZ=0
    g4: ArcOfCircle CenterX=-64 CenterY=15 CenterZ=0 NormalX=0 NormalY=0 NormalZ=1 AngleXU=0 Radius=1.75 StartAngle=1.5708 EndAngle=4.71239
    g5: ArcOfCircle CenterX=-61 CenterY=15 CenterZ=0 NormalX=0 NormalY=0 NormalZ=1 AngleXU=0 Radius=1.75 StartAngle=4.71239 EndAngle=7.85398
    g6: LineSegment StartX=-64 StartY=13.25 StartZ=0 EndX=-61 EndY=13.25 EndZ=0
    g7: LineSegment StartX=-64 StartY=16.75 StartZ=0 EndX=-61 EndY=16.75 EndZ=0
  constraints (20):
    c: Tangent(g0,g3) = 1.5708
    c: Tangent(g0,g2) = -1.5708
    c: Tangent(g2,g1) = -1.5708
    c: Tangent(g3,g1) = 1.5708
    c: Horizontal(g2)
    c: Equal(g0,g1)
    c: DistanceY(g1,g1) = 3.5
    c: DistanceY(g-1,g0) = 15
    c: Tangent(g4,g7) = 1.5708
    c: Tangent(g4,g6) = -1.5708
    c: Tangent(g6,g5) = -1.5708
    c: Tangent(g7,g5) = 1.5708
    c: Horizontal(g6)
    c: Equal(g4,g5)
    c: Equal(g1,g5) = 3.5
    c: DistanceX(g1,g5) = 20
    c: DistanceX(g0,g1) = 3
    c: DistanceX(g4,g-1) = 64
    c: Horizontal(g0,g4)
    c: DistanceX(g4,g5) = 3
FEATURE [PartDesign::Pocket] Pocket004
  BaseFeature = -> Fillet
  Length = 5
  Length2 = 100
  Profile = -> Sketch008
  Type = 0
FEATURE [PartDesign::Body] Body
  Group = -> [Sketch,Pad,Sketch001,Pad001,Sketch002,Pocket,Sketch005,Pocket002,Sketch006,Pad003,Sketch007,Pocket003,Fillet,Sketch008,Pocket004]
  Origin = -> Origin
  Tip = -> Pocket004
FEATURE [Sketcher::SketchObject] Sketch009
  FullyConstrained = false
  MapMode = 5
  Support = -> [XY_Plane002]
  sketch-geometry (12):
    g0: LineSegment StartX=205.301 StartY=67.9854 StartZ=0 EndX=242.583 EndY=67.9854 EndZ=0
    g1: LineSegment StartX=245.301 StartY=65.2675 StartZ=0 EndX=245.301 EndY=23.9854 EndZ=0
    g2: LineSegment StartX=245.301 StartY=23.9854 StartZ=0 EndX=205.301 EndY=23.9854 EndZ=0
    g3: LineSegment StartX=205.301 StartY=23.9854 StartZ=0 EndX=205.301 EndY=67.9854 EndZ=0
    g4: ArcOfCircle CenterX=242.583 CenterY=65.2675 CenterZ=0 NormalX=0 NormalY=0 NormalZ=1 AngleXU=0 Radius=2.71788 StartAngle=-9e-16 EndAngle=1.5708
    g5: Circle CenterX=235.301 CenterY=53.9854 CenterZ=0 NormalX=0 NormalY=0 NormalZ=1 AngleXU=0 Radius=2.8
    g6: Circle CenterX=235.301 CenterY=33.9854 CenterZ=0 NormalX=0 NormalY=0 NormalZ=1 AngleXU=0 Radius=2.8
    g7: LineSegment StartX=235.301 StartY=53.9854 StartZ=0 EndX=235.301 EndY=33.9854 EndZ=0
    g8: Circle CenterX=215.301 CenterY=53.9854 CenterZ=0 NormalX=0 NormalY=0 NormalZ=1 AngleXU=0 Radius=2.8
    g9: LineSegment StartX=235.301 StartY=53.9854 StartZ=0 EndX=215.301 EndY=53.9854 EndZ=0
    g10: Circle CenterX=215.301 CenterY=33.9854 CenterZ=0 NormalX=0 NormalY=0 NormalZ=1 AngleXU=0 Radius=2.8
    g11: LineSegment StartX=215.301 StartY=53.9854 StartZ=0 EndX=215.301 EndY=33.9854 EndZ=0
  constraints (29):
    c: Coincident(g1,g2)
    c: Coincident(g2,g3)
    c: Coincident(g3,g0)
    c: Horizontal(g0)
    c: Horizontal(g2)
    c: Vertical(g1)
    c: Vertical(g3)
    c: Tangent(g0,g4) = 1.5708
    c: Tangent(g1,g4) = 1.5708
    c: DistanceX(g0,g1) = 40
    c: DistanceY(g1,g0) = 44
    c: Radius(g5) = 2.8
    c: Radius(g6) = 2.8
    c: Coincident(g5,g7)
    c: Coincident(g6,g7)
    c: Distance(g7) = 20
    c: Angle(g7) = -1.5708
    c: Radius(g8) = 2.8
    c: Coincident(g5,g9)
    c: Coincident(g8,g9)
    c: Equal(g9,g7)
    c: Perpendicular(g9,g7)
    c: Radius(g10) = 2.8
    c: Coincident(g8,g11)
    c: Coincident(g10,g11)
    c: Equal(g7,g11)
    c: Parallel(g11,g7)
    c: DistanceY(g1,g6) = 10
    c: DistanceX(g6,g1) = 10
FEATURE [PartDesign::Pad] Pad004
  Direction = (1,1,1)
  Length = 4
  Length2 = 100
  Profile = -> Sketch009
  Type = 0
FEATURE [PartDesign::Body] Body002  label="Spacer - 4mm"
  Group = -> [Sketch009,Pad004]
  Origin = -> Origin002
  Tip = -> Pad004
